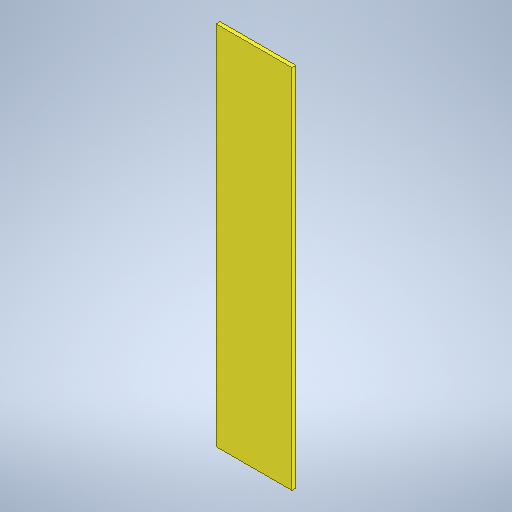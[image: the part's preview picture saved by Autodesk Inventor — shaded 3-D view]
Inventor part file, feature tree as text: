
AUTODESK INVENTOR PART (.ipt)
format: ipt  version: 2025.1 (Build 291241020, 241B)  size: 256,000 bytes
history: native  units: in
note: dims shown in document units (in); Inventor stores cm internally (conversion verified against a paired STEP export)
features: extrude x1, sketch x1
ambient origin geometry x8: Origin, YZ Plane, XZ Plane, XY Plane, X Axis, Y Axis, Z Axis, Center Point
bodies: Solid1 (feature_tree)
feature tree (2):
  extrude  "Extrusion1"  Depth=12.0in
  sketch  "Sketch1"  dims[d2=57.9155in d3=12.0in d4=0.625in d5=0.0in]
